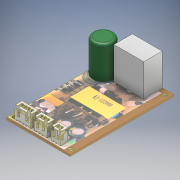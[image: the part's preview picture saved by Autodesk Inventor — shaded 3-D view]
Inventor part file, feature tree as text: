
AUTODESK INVENTOR PART (.ipt)
format: ipt  version: 2017 (Build 210142000, 142)  size: 1,916,928 bytes
history: native  units: mm
features: other x15, sketch x6, extrude x3, hole x1, fillet x1
ambient origin geometry x8: Origin, YZ Plane, XZ Plane, XY Plane, X Axis, Y Axis, Z Axis, Center Point
bodies: Solide1 (feature_tree), Solide2 (feature_tree), Solide3 (feature_tree), Solide4 (feature_tree), Solide5 (feature_tree)
feature tree (26):
  other  "Connecteur jst 2 broches.iam"
  other  "Connecteur jst 4 broches.iam"
  other  "Connecteur jst 3 broches.iam"
  other  "Connecteur jst 2 broches femelle.ipt:1"
  other  "Connecteur JST 2 Broches Male.ipt:1"
  other  "Connecteur jst 4 broches femelle.ipt:1"
  other  "Connecteur JST 4 Broches Male.ipt:1"
  other  "Connecteur jst 3 broches femelle.ipt:1"
  other  "Connecteur JST 3 Broches Male.ipt:1"
  extrude  "Extrusion1"  Depth=50.0mm
  hole  "Perçage1"  [1 undecoded]
  extrude  "Extrusion2"  Depth=1.5mm TaperAngle=0.0deg
  extrude  "Extrusion3"  Depth=74.0mm
  other  "Décalcomanie1"
  fillet  "Congé1"  Radius=44.0mm
  other  "Déplacer des corps1"
  other  "Déplacer des corps2"
  other  "Déplacer des corps3"
  other  "Combiner1"
  sketch  "Esquisse8"
  sketch  "Esquisse1"
  sketch  "Esquisse2"
  sketch  "Esquisse3"
  sketch  "Esquisse4"
  sketch  "Esquisse6"
  other  "Image1"
note: 1 required parameter value undecoded (feature->parameter linkage not recoverable at this tier; creation-order binding heuristic only, values carry confidence <= 0.55)
